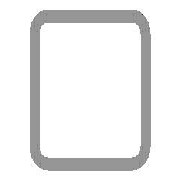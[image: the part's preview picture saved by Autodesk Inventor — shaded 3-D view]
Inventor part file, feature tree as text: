
AUTODESK INVENTOR PART (.ipt)
format: ipt  version: 2018 (Build 220112000, 112)  size: 129,536 bytes
history: native  units: mm (DEFAULTED — no unit token found)
features: other x4, sketch x3, extrude x1, plane x1
ambient origin geometry x8: Origin, YZ Plane, XZ Plane, XY Plane, X Axis, Y Axis, Z Axis, Center Point
bodies: Solid1 (feature_tree)
feature tree (9):
  other  "Tubolare horizontal corto"
  other  "Driven Length"
  other  "Piano iniziale"
  other  "Piano finale"
  extrude  "Corpo"  TaperAngle=0.0deg  [1 undecoded]
  sketch  "Schizzo"
  sketch  "Sketch3"  dims[d3=300.0mm d4=0.0mm]
  plane  "Work Plane3"
  sketch  "Sketch4"  dims[d7=4.0mm d9=40.0mm d11=40.0mm d12=2.0mm d13=-0.0mm d14=300.0mm d15=20.0mm d16=20.0mm d17=90.0deg d18=300.0mm]
note: 1 required parameter value undecoded (feature->parameter linkage not recoverable at this tier; creation-order binding heuristic only, values carry confidence <= 0.55)
